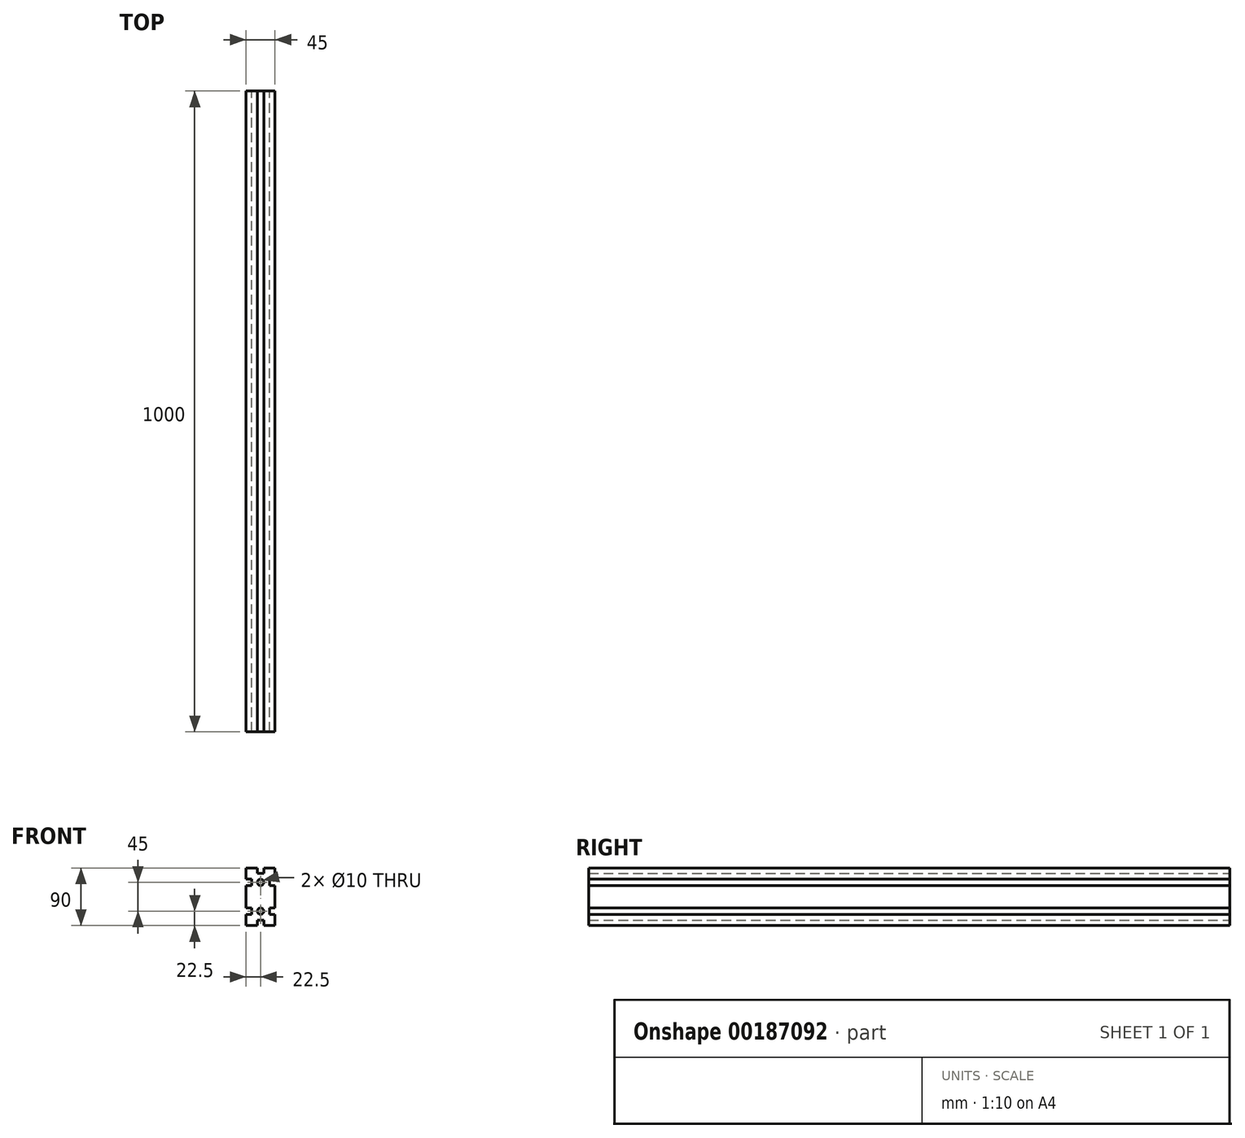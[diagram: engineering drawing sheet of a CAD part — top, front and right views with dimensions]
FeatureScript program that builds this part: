
annotation { "Feature Type Name" : "Feature", "Feature Type Description" : "" }
export const myFeature = defineFeature(function(context is Context, id is Id, definition is map)
    precondition{}
    {
        {
            var Q0;
            Q0=qCreatedBy(makeId("Front.planeOp"),FACE);
            var sketch = newSketch(context, id + "F0", { "sketchPlane" : qUnion([Q0])});
            skLineSegment(sketch, "E0.bottom", {"start": v(22.5, -45) * mm, "end": v(5, -45) * mm});
            skLineSegment(sketch, "E0.top", {"start": v(22.5, 45) * mm, "end": v(5, 45) * mm});
            skLineSegment(sketch, "E0.left", {"start": v(22.5, -45) * mm, "end": v(22.5, -27.5) * mm});
            skLineSegment(sketch, "E0.right", {"start": v(-22.5, -45) * mm, "end": v(-22.5, -27.5) * mm});
            skPoint(sketch, "E0.middle", {"position": v(0, 0) * mm});
            skCircle(sketch, "E1", {"center": v(0, 22.5) * mm, "radius": 5 * mm});
            skCircle(sketch, "E2", {"center": v(0, -22.5) * mm, "radius": 5 * mm});
            skLineSegment(sketch, "E3", {"start": v(-5, 45) * mm, "end": v(-5, 36.25) * mm});
            skLineSegment(sketch, "E4", {"start": v(5, 45) * mm, "end": v(5, 36.25) * mm});
            skLineSegment(sketch, "E5", {"start": v(-22.5, 27.5) * mm, "end": v(-13.75, 27.5) * mm});
            skLineSegment(sketch, "E6", {"start": v(-22.5, 17.5) * mm, "end": v(-13.75, 17.5) * mm});
            skLineSegment(sketch, "E7", {"start": v(-22.5, -17.5) * mm, "end": v(-13.75, -17.5) * mm});
            skLineSegment(sketch, "E8", {"start": v(-22.5, -27.5) * mm, "end": v(-13.75, -27.5) * mm});
            skLineSegment(sketch, "E9", {"start": v(-13.75, 27.5) * mm, "end": v(-13.75, 17.5) * mm});
            skLineSegment(sketch, "E10", {"start": v(13.75, 27.5) * mm, "end": v(13.75, 17.5) * mm});
            skLineSegment(sketch, "E11", {"start": v(-5, 36.25) * mm, "end": v(5, 36.25) * mm});
            skPoint(sketch, "E12.orphan", {"position": v(-22.5, 36.25) * mm});
            skLineSegment(sketch, "E13.trimOffspring", {"start": v(13.75, 17.5) * mm, "end": v(22.5, 17.5) * mm});
            skLineSegment(sketch, "E14.trimOffspring", {"start": v(-22.5, 27.5) * mm, "end": v(-22.5, 45) * mm});
            skLineSegment(sketch, "E15.trimOffspring", {"start": v(-13.75, -17.5) * mm, "end": v(-13.75, -27.5) * mm});
            skLineSegment(sketch, "E16.trimOffspring", {"start": v(13.75, 27.5) * mm, "end": v(22.5, 27.5) * mm});
            skLineSegment(sketch, "E17.trimOffspring", {"start": v(22.5, 27.5) * mm, "end": v(22.5, 45) * mm});
            skLineSegment(sketch, "E18.trimOffspring", {"start": v(-5, 45) * mm, "end": v(-22.5, 45) * mm});
            skLineSegment(sketch, "E19.trimOffspring", {"start": v(13.75, -17.5) * mm, "end": v(13.75, -27.5) * mm});
            skLineSegment(sketch, "E20.trimOffspring", {"start": v(13.75, -17.5) * mm, "end": v(22.5, -17.5) * mm});
            skLineSegment(sketch, "E21.trimOffspring", {"start": v(-5, -36.25) * mm, "end": v(-5, -45) * mm});
            skLineSegment(sketch, "E22.trimOffspring", {"start": v(13.75, -27.5) * mm, "end": v(22.5, -27.5) * mm});
            skLineSegment(sketch, "E23.trimOffspring", {"start": v(5, -36.25) * mm, "end": v(5, -45) * mm});
            skLineSegment(sketch, "E24.trimOffspring", {"start": v(22.5, -17.5) * mm, "end": v(22.5, 17.5) * mm});
            skLineSegment(sketch, "E25.trimOffspring", {"start": v(-22.5, -17.5) * mm, "end": v(-22.5, 17.5) * mm});
            skLineSegment(sketch, "E26.trimOffspring", {"start": v(-5, -45) * mm, "end": v(-22.5, -45) * mm});
            skPoint(sketch, "E27.orphan", {"position": v(13.75, -45) * mm});
            skLineSegment(sketch, "E28.trimOffspring", {"start": v(-5, -36.25) * mm, "end": v(5, -36.25) * mm});
            skPoint(sketch, "E29.start.orphan", {"position": v(-22.5, -36.25) * mm});
            skPoint(sketch, "E30.trimOffspring.end.orphan", {"position": v(-13.75, -45) * mm});
            skSolve(sketch);
        }
        {
            var Q0;
            Q0=makeQuery(id+"F0.imprint","IMPRINT",FACE,{"disambiguationData":[TD([[makeQuery(id+"F0.imprint","IMPRINT",EDGE,{"derivedFrom":sQuery(id+"F0.wireOp",EDGE,"E0.bottom")}),-1.0]])]});
            extrude(context, id + "F1", {"entities" : qUnion([Q0]), "depth" : 1000 * mm});
        }
    });
